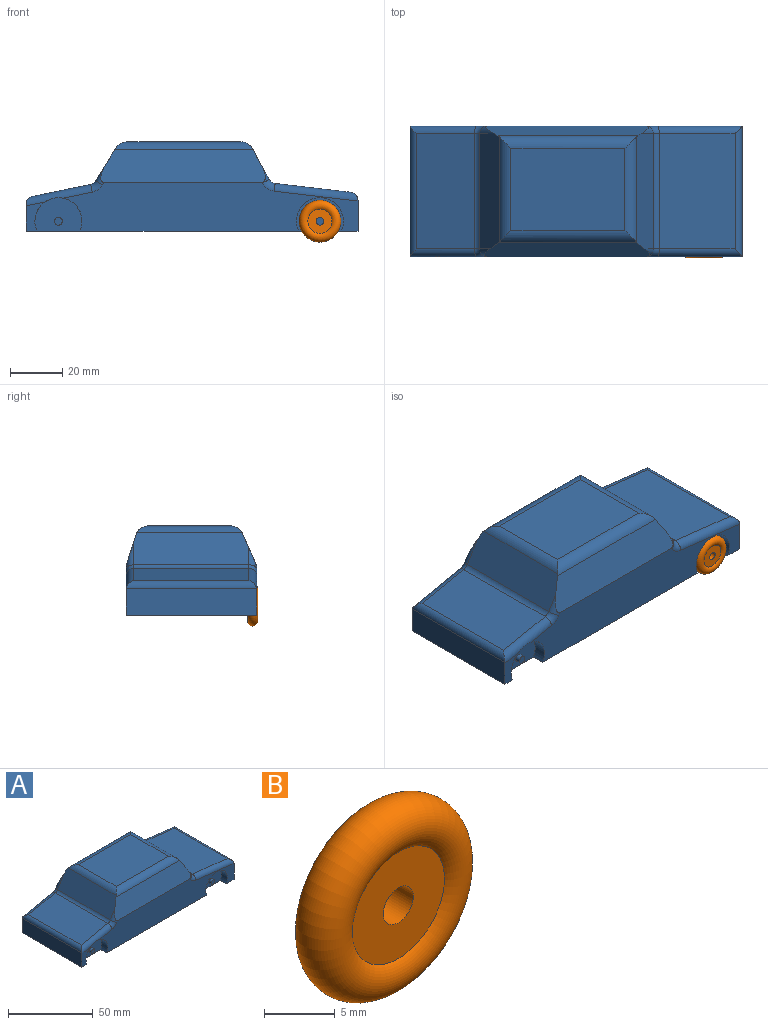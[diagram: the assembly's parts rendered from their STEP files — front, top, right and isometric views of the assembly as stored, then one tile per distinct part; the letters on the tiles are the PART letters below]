
ASSEMBLY  parts=2 mates=1
PART A: 46 faces, bbox 127.9x50x34.1 mm
  f0: plane 11.19x7.27mm, normal (0,1,0), area 42.1mm2, adj f6,f7,f18,f34
  f1: plane 112.78x18.7mm, normal (0,-1,0), area 1593mm2, adj f7,f8,f12,f14,f17,f31,f32,f33
  f2: plane 112.78x18.78mm, normal (0,1,0), area 1597.8mm2, adj f7,f8,f16,f18,f20,f26,f27,f28
  f3: plane 44.01x11.77mm, normal (0.88,0,0.48), area 578.7mm2, adj f16,f17,f22,f23,f25,f26,f30,f33
  f4: plane 43.58x31.41mm, normal (0,0,1), area 1369mm2, adj f22,f23,f24,f25
  f5: plane 44.02x12.5mm, normal (-0.85,0,0.52), area 630.9mm2, adj f16,f17,f22,f24,f25,f35,f39,f41
  f6: plane 50x10.31mm, normal (-1,0,0), area 515.5mm2, adj f0,f7,f11,f34,f36,f38
  f7: plane 126.95x50mm, normal (0,0,-1), area 6021mm2, adj f0,f1,f2,f6,f8,f11,f12,f13
  f8: plane 50x11.86mm, normal (1,0,0), area 593.1mm2, adj f1,f2,f7,f27,f29,f31
  f9: plane 44x29.03mm, normal (0.12,0,0.99), area 1285.7mm2, adj f27,f29,f30,f31
  f10: plane 44x22.35mm, normal (-0.2,0,0.98), area 1004.1mm2, adj f34,f36,f38,f39
  f11: plane 11.19x7.27mm, normal (0,-1,0), area 42.1mm2, adj f6,f7,f14,f38
  f12: cylinder r=9mm len=18mm, axis (0,-1,0), area 180.5mm2, adj f1,f7,f13
  f13: plane 18x12.79mm, normal (0,-1,0), area 186.3mm2, adj f7,f12,f44
  f14: cylinder r=9mm len=18mm, axis (0,-1,0), area 180.2mm2, adj f1,f7,f11,f15,f38
  f15: plane 18x12.79mm, normal (0,-1,0), area 186.3mm2, adj f7,f14,f42
  f16: plane 62.18x11.85mm, normal (0,0.95,0.3), area 734.4mm2, adj f2,f3,f5,f22,f26,f35
  f17: plane 62.87x12.43mm, normal (0,-0.92,0.4), area 803.6mm2, adj f1,f3,f5,f25,f33,f41
  f18: cylinder r=9mm len=18mm, axis (0,1,0), area 180.2mm2, adj f0,f2,f7,f19,f34
  f19: plane 18x12.79mm, normal (0,1,0), area 193.4mm2, adj f7,f18
  f20: cylinder r=9mm len=18mm, axis (0,1,0), area 180.5mm2, adj f2,f7,f21
  f21: plane 18x12.79mm, normal (0,1,0), area 193.4mm2, adj f7,f20
  f22: cylinder r=5mm len=53.38mm, axis (-1,0,0), area 310mm2, adj f3,f4,f5,f16,f23,f24
  f23: cylinder r=5mm len=40.18mm, axis (0,1,0), area 194.1mm2, adj f3,f4,f22,f25
  f24: cylinder r=5mm len=39.95mm, axis (0,1,0), area 184.6mm2, adj f4,f5,f22,f25
  f25: cylinder r=5mm len=52.81mm, axis (1,0,0), area 281.7mm2, adj f3,f4,f5,f17,f23,f24
  f26: cylinder r=3mm len=9.88mm, axis (-0.48,0,0.88), area 16mm2, adj f2,f3,f16,f28
  f27: cylinder r=3mm len=32.37mm, axis (-0.99,0,0.12), area 146.7mm2, adj f2,f8,f9,f28,f29
  f28: torus R=6mm, axis (0,-1,0), area 18.4mm2, adj f2,f26,f27,f30
  f29: cylinder r=3mm len=49.96mm, axis (0,1,0), area 208mm2, adj f8,f9,f27,f31
  f30: cylinder r=3mm len=44mm, axis (0,-1,0), area 126mm2, adj f3,f9,f28,f32
  f31: cylinder r=3mm len=32.37mm, axis (0.99,0,-0.12), area 146.7mm2, adj f1,f8,f9,f29,f32
  f32: torus R=6mm, axis (0,-1,0), area 18.4mm2, adj f1,f30,f31,f33
  f33: cylinder r=3mm len=7.2mm, axis (0.48,0,-0.88), area 10.5mm2, adj f1,f3,f17,f32
  f34: cylinder r=3mm len=25.96mm, axis (-0.98,0,-0.2), area 113.1mm2, adj f0,f2,f6,f10,f18,f36,f37
  f35: cylinder r=3mm len=10.52mm, axis (-0.52,0,-0.85), area 19.5mm2, adj f2,f5,f16,f37
  f36: cylinder r=3mm len=49.88mm, axis (0,1,0), area 194.8mm2, adj f6,f10,f34,f38
  f37: torus R=6mm, axis (0,-1,0), area 15.8mm2, adj f2,f34,f35,f39
  f38: cylinder r=3mm len=25.96mm, axis (0.98,0,0.2), area 113.1mm2, adj f1,f6,f10,f11,f14,f36,f40
  f39: cylinder r=3mm len=44mm, axis (0,-1,0), area 108.2mm2, adj f5,f10,f37,f40
  f40: torus R=6mm, axis (0,-1,0), area 15.8mm2, adj f1,f38,f39,f41
  f41: cylinder r=3mm len=7.84mm, axis (0.52,0,0.85), area 13.8mm2, adj f1,f5,f17,f40
  f42: cylinder r=1.5mm len=3mm, axis (0,1,0), area 18.8mm2, adj f15,f43
  f43: plane 3x3mm, normal (0,-1,0), area 7.1mm2, adj f42
  f44: cylinder r=1.5mm len=3mm, axis (0,1,0), area 18.8mm2, adj f13,f45
  f45: plane 3x3mm, normal (0,-1,0), area 7.1mm2, adj f44
PART B: 4 faces, bbox 17.3x2.9x17.3 mm
  f0: plane 9.2x9.2mm, normal (0,1,0), area 59.4mm2, adj f1,f3
  f1: torus R=6mm, axis (0,1,0), area 389.7mm2, adj f0,f2
  f2: plane 9.2x9.2mm, normal (0,-1,0), area 59.4mm2, adj f1,f3
  f3: cylinder r=1.5mm len=3mm, axis (0,1,0), area 26.9mm2, adj f0,f2
PLACE A t=(15.65,-30.98,-57.5)mm
PLACE B t=(96.48,-80.83,-44.36)mm
MATE slider A.f12 <-> B.f1  axis (0,-1,0) through (82.88,-77.98,-44.36)mm
